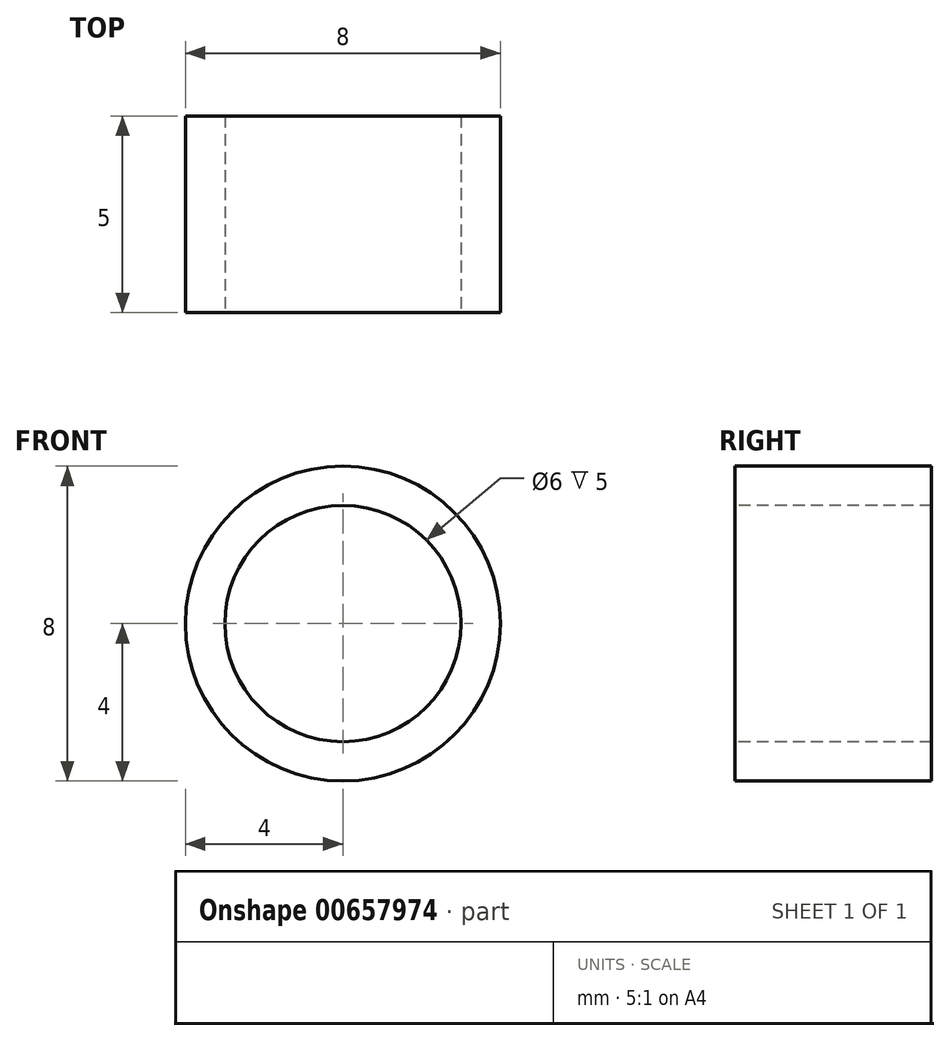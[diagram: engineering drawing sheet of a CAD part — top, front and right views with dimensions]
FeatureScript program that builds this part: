
annotation { "Feature Type Name" : "Feature", "Feature Type Description" : "" }
export const myFeature = defineFeature(function(context is Context, id is Id, definition is map)
    precondition{}
    {
        {
            var Q0;
            Q0=qCreatedBy(makeId("Right.planeOp"),FACE);
            var sketch = newSketch(context, id + "F0", { "sketchPlane" : qUnion([Q0])});
            skLineSegment(sketch, "E0.bottom", {"start": v(2.5, 3) * mm, "end": v(-2.5, 3) * mm});
            skLineSegment(sketch, "E0.top", {"start": v(2.5, 4) * mm, "end": v(-2.5, 4) * mm});
            skLineSegment(sketch, "E0.left", {"start": v(2.5, 3) * mm, "end": v(2.5, 4) * mm});
            skLineSegment(sketch, "E0.right", {"start": v(-2.5, 3) * mm, "end": v(-2.5, 4) * mm});
            skPoint(sketch, "E0.middle", {"position": v(0, 3.5) * mm});
            skLineSegment(sketch, "E1", {"start": v(-3.4, 0) * mm, "end": v(3.9, 0) * mm, "construction": true});
            skSolve(sketch);
        }
        {
            var Q0;
            Q0=makeQuery(id+"F0.imprint","IMPRINT",FACE,{"disambiguationData":[TD([[makeQuery(id+"F0.imprint","IMPRINT",EDGE,{"derivedFrom":sQuery(id+"F0.wireOp",EDGE,"E0.bottom")}),-1.0]])]});
            var Q1;
            Q1=sQuery(id+"F0.wireOp",EDGE,"E1");
            revolve(context, id + "F1", {"entities" : qUnion([Q0]), "axis" : qUnion([Q1]), "revolveType" : RevolveType.FULL});
        }
    });
